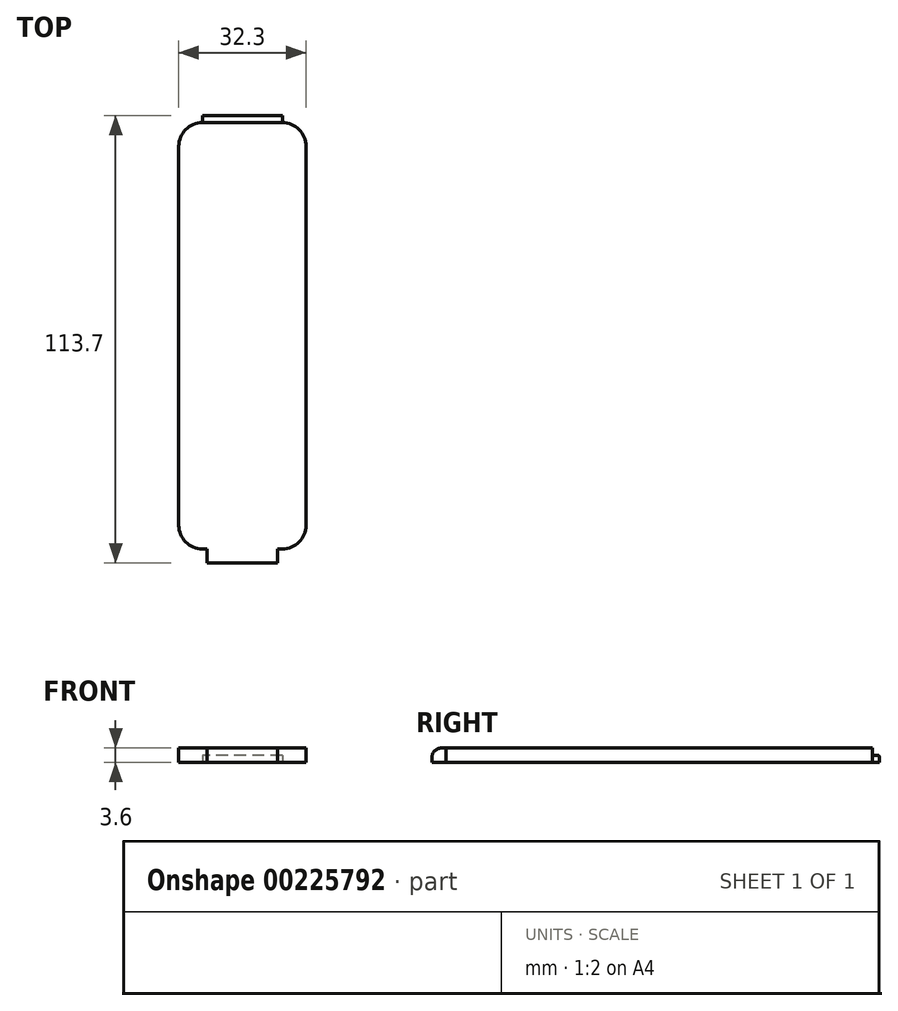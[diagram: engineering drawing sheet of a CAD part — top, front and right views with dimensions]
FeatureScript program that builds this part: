
annotation { "Feature Type Name" : "Feature", "Feature Type Description" : "" }
export const myFeature = defineFeature(function(context is Context, id is Id, definition is map)
    precondition{}
    {
        {
            assignVariable(context, id + "F0", {"name" : "O", "anyValue" : 3.6});
        }
        {
            var Q0;
            Q0=qCreatedBy(makeId("Top.planeOp"),FACE);
            var sketch = newSketch(context, id + "F1", { "sketchPlane" : qUnion([Q0])});
            skLineSegment(sketch, "E0.bottom", {"start": v(10.15, -54.15) * mm, "end": v(-10.15, -54.15) * mm});
            skLineSegment(sketch, "E0.top", {"start": v(10.15, 54.15) * mm, "end": v(-10.15, 54.15) * mm});
            skLineSegment(sketch, "E0.left", {"start": v(16.15, -48.15) * mm, "end": v(16.15, 48.15) * mm});
            skLineSegment(sketch, "E0.right", {"start": v(-16.15, -48.15) * mm, "end": v(-16.15, 48.15) * mm});
            skPoint(sketch, "E0.middle", {"position": v(0, 0) * mm});
            skPoint(sketch, "E1.visualSharp", {"position": v(16.15, 54.15) * mm});
            skArc(sketch, "E1.filletArc", {"start": v(16.15, 48.15) * mm, "mid": v(14.4, 52.4) * mm, "end": v(10.15, 54.15) * mm});
            skPoint(sketch, "E2.visualSharp", {"position": v(-16.15, 54.15) * mm});
            skArc(sketch, "E2.filletArc", {"start": v(-10.15, 54.15) * mm, "mid": v(-14.4, 52.4) * mm, "end": v(-16.15, 48.15) * mm});
            skPoint(sketch, "E3.visualSharp", {"position": v(-16.15, -54.15) * mm});
            skArc(sketch, "E3.filletArc", {"start": v(-16.15, -48.15) * mm, "mid": v(-14.4, -52.4) * mm, "end": v(-10.15, -54.15) * mm});
            skPoint(sketch, "E4.visualSharp", {"position": v(16.15, -54.15) * mm});
            skArc(sketch, "E4.filletArc", {"start": v(10.15, -54.15) * mm, "mid": v(14.4, -52.4) * mm, "end": v(16.15, -48.15) * mm});
            skSolve(sketch);
        }
        {
            var Q0;
            Q0=makeQuery(id+"F1.imprint","IMPRINT",FACE,{"disambiguationData":[TD([[makeQuery(id+"F1.imprint","IMPRINT",EDGE,{"derivedFrom":sQuery(id+"F1.wireOp",EDGE,"E0.bottom")}),-1.0]])]});
            extrude(context, id + "F2", {"entities" : qUnion([Q0]), "depth" : (getVariable(context, 'O')) * mm});
        }
        {
            var Q0;
            Q0=makeQuery(id+"F2.opExtrude","SWEPT_FACE",FACE,{"disambiguationData":[OSD([sQuery(id+"F1.wireOp",EDGE,"E0.bottom")])]});
            var sketch = newSketch(context, id + "F3", { "sketchPlane" : qUnion([Q0])});
            skLineSegment(sketch, "E5.bottom", {"start": v(-9, 3.6) * mm, "end": v(9, 3.6) * mm});
            skLineSegment(sketch, "E5.top", {"start": v(-9, 0) * mm, "end": v(9, 0) * mm});
            skLineSegment(sketch, "E5.left", {"start": v(-9, 3.6) * mm, "end": v(-9, 0) * mm});
            skLineSegment(sketch, "E5.right", {"start": v(9, 3.6) * mm, "end": v(9, 0) * mm});
            skLineSegment(sketch, "E6", {"start": v(-10.15, 1.8) * mm, "end": v(-9, 1.8) * mm});
            skLineSegment(sketch, "E7", {"start": v(9, 1.8) * mm, "end": v(10.15, 1.8) * mm});
            skSolve(sketch);
        }
        {
            var Q0;
            Q0=makeQuery(id+"F3.imprint","IMPRINT",FACE,{"disambiguationData":[TD([[makeQuery(id+"F3.imprint","IMPRINT",EDGE,{"derivedFrom":sQuery(id+"F3.wireOp",EDGE,"E5.bottom")}),1.0]])]});
            extrude(context, id + "F4", {"entities" : qUnion([Q0]), "operationType" : NewBodyOperationType.ADD, "depth" : 3.6 * mm});
        }
        {
            var Q0;
            Q0=makeQuery(id+"F2.opExtrude","SWEPT_FACE",FACE,{"disambiguationData":[OSD([sQuery(id+"F1.wireOp",EDGE,"E0.top")])]});
            var sketch = newSketch(context, id + "F5", { "sketchPlane" : qUnion([Q0])});
            skLineSegment(sketch, "E8", {"start": v(-10.15, 1.8) * mm, "end": v(10.15, 1.8) * mm});
            skSolve(sketch);
        }
        {
            var Q0;
            {var subQ0=sQuery(id+"F5.wireOp",EDGE,"E8");Q0=makeQuery(id+"F5.imprint","IMPRINT",FACE,{"disambiguationData":[TD([[makeQuery(id+"F5.imprint","IMPRINT",EDGE,{"derivedFrom":subQ0}),-1.0]])]});}
            extrude(context, id + "F6", {"entities" : qUnion([Q0]), "operationType" : NewBodyOperationType.ADD, "depth" : (3.6 / 2) * mm});
        }
        {
            var Q0;
            Q0=makeQuery(id+"F4.opExtrude","CAP_EDGE",EDGE,{"disambiguationData":[OSD([sQuery(id+"F3.wireOp",EDGE,"E5.bottom")])],"isStart":false});
            fillet(context, id + "F7", {"entities" : qUnion([Q0]), "radius" : getVariable(context, 'O') * 0.66 * mm, "tangentPropagation" : true, "allowEdgeOverflow" : false});
        }
        {
            var Q0;
            Q0=makeQuery(id+"F6.opExtrude","CAP_EDGE",EDGE,{"disambiguationData":[OSD([sQuery(id+"F5.wireOp",EDGE,"E8")])],"isStart":false});
            fillet(context, id + "F8", {"entities" : qUnion([Q0]), "radius" : .5 * mm, "tangentPropagation" : true, "allowEdgeOverflow" : false});
        }
    });
